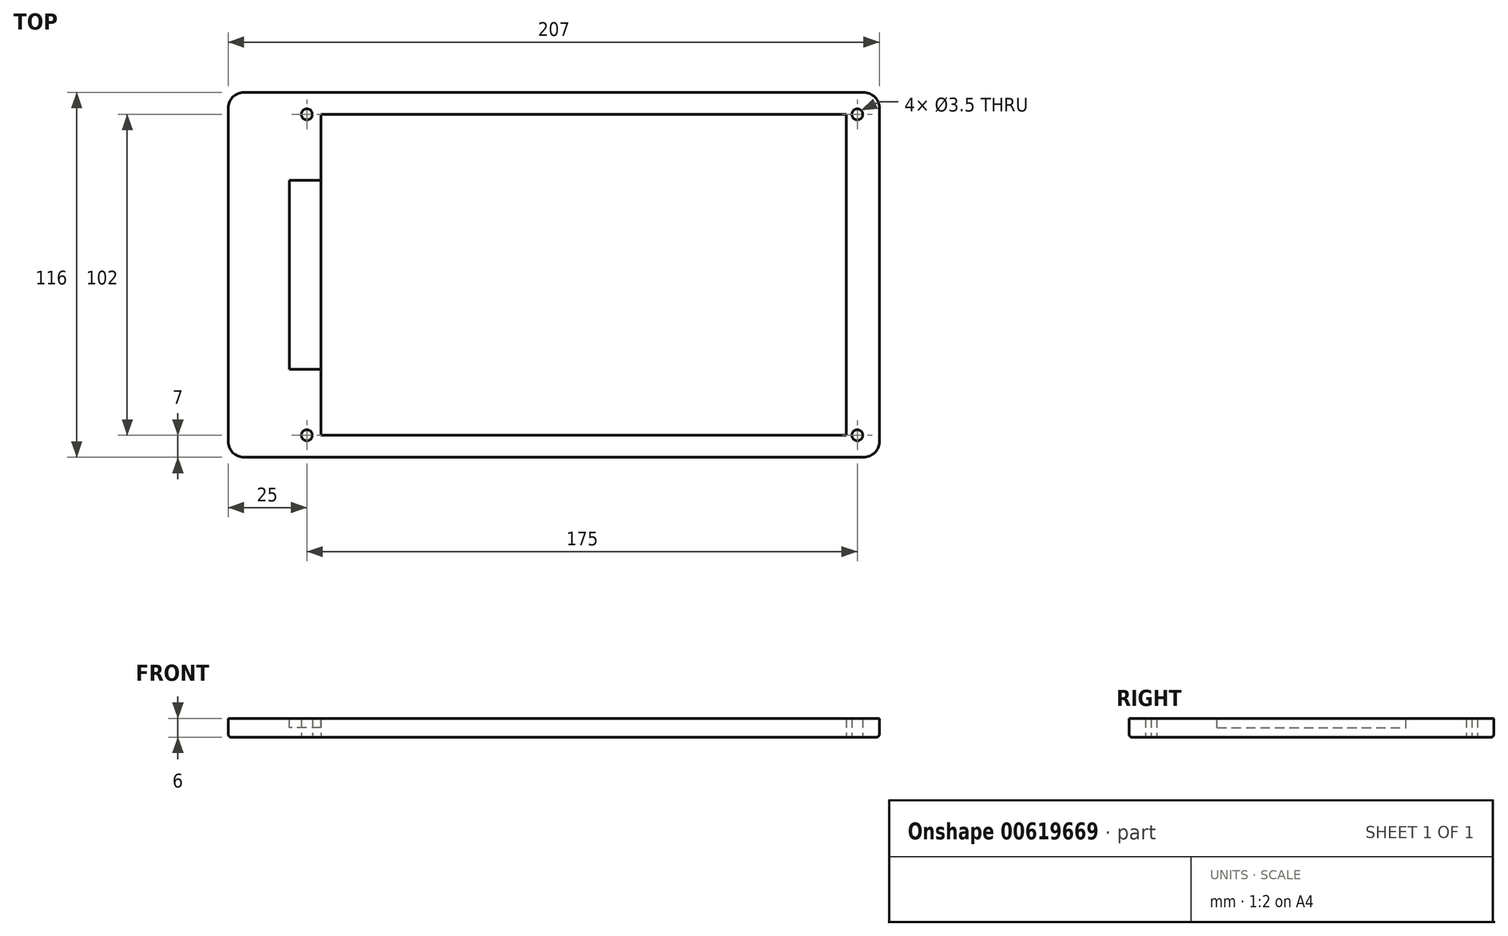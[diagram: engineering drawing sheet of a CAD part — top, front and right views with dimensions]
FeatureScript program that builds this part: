
annotation { "Feature Type Name" : "Feature", "Feature Type Description" : "" }
export const myFeature = defineFeature(function(context is Context, id is Id, definition is map)
    precondition{}
    {
        {
            var Q0;
            Q0=qCreatedBy(makeId("Top.planeOp"),FACE);
            var sketch = newSketch(context, id + "F0", { "sketchPlane" : qUnion([Q0])});
            skLineSegment(sketch, "E0.bottom", {"start": v(0, 0) * mm, "end": v(207, 0) * mm});
            skLineSegment(sketch, "E0.top", {"start": v(0, -116) * mm, "end": v(207, -116) * mm});
            skLineSegment(sketch, "E0.left", {"start": v(0, 0) * mm, "end": v(0, -116) * mm});
            skLineSegment(sketch, "E0.right", {"start": v(207, 0) * mm, "end": v(207, -116) * mm});
            skSolve(sketch);
        }
        {
            var Q0;
            Q0=makeQuery(id+"F0.imprint","IMPRINT",FACE,{"disambiguationData":[TD([[makeQuery(id+"F0.imprint","IMPRINT",EDGE,{"derivedFrom":sQuery(id+"F0.wireOp",EDGE,"E0.bottom")}),-1.0]])]});
            extrude(context, id + "F1", {"entities" : qUnion([Q0]), "depth" : 6 * mm, "offsetDistance" : 25 * mm});
        }
        {
            var Q0;
            Q0=makeQuery(id+"F0.imprint","IMPRINT",FACE,{"disambiguationData":[TD([[makeQuery(id+"F0.imprint","IMPRINT",EDGE,{"derivedFrom":sQuery(id+"F0.wireOp",EDGE,"E0.bottom")}),-1.0]])]});
            var sketch = newSketch(context, id + "F2", { "sketchPlane" : qUnion([Q0])});
            skLineSegment(sketch, "E1.bottom", {"start": v(29.5, -7) * mm, "end": v(196.5, -7) * mm});
            skLineSegment(sketch, "E1.top", {"start": v(29.5, -109) * mm, "end": v(196.5, -109) * mm});
            skLineSegment(sketch, "E1.left", {"start": v(29.5, -7) * mm, "end": v(29.5, -109) * mm});
            skLineSegment(sketch, "E1.right", {"start": v(196.5, -7) * mm, "end": v(196.5, -109) * mm});
            skSolve(sketch);
        }
        {
            var Q0;
            Q0=makeQuery(id+"F2.imprint","IMPRINT",FACE,{"disambiguationData":[TD([[makeQuery(id+"F2.imprint","IMPRINT",EDGE,{"derivedFrom":sQuery(id+"F2.wireOp",EDGE,"E1.bottom")}),-1.0]])]});
            extrude(context, id + "F3", {"entities" : qUnion([Q0]), "operationType" : NewBodyOperationType.REMOVE, "depth" : 25 * mm, "offsetDistance" : 25 * mm});
        }
        {
            var Q0;
            Q0=makeQuery(id+"F1.opExtrude","CAP_FACE",FACE,{"disambiguationData":[OSD([sQuery(id+"F0.wireOp",EDGE,"E0.bottom"),sQuery(id+"F0.wireOp",EDGE,"E0.top"),sQuery(id+"F0.wireOp",EDGE,"E0.left"),sQuery(id+"F0.wireOp",EDGE,"E0.right")])],"isStart":true});
            var sketch = newSketch(context, id + "F4", { "sketchPlane" : qUnion([Q0])});
            skLineSegment(sketch, "E2", {"start": v(207, 7) * mm, "end": v(0, 7) * mm, "construction": true});
            skCircle(sketch, "E3", {"center": v(200, 7) * mm, "radius": 1.75 * mm});
            skCircle(sketch, "E4", {"center": v(25, 7) * mm, "radius": 1.75 * mm});
            skLineSegment(sketch, "E5", {"start": v(207, 109) * mm, "end": v(0, 109) * mm, "construction": true});
            skCircle(sketch, "E6", {"center": v(200, 109) * mm, "radius": 1.75 * mm});
            skCircle(sketch, "E7", {"center": v(25, 109) * mm, "radius": 1.75 * mm});
            skSolve(sketch);
        }
        {
            var Q0;
            Q0=makeQuery(id+"F4.imprint","IMPRINT",FACE,{"disambiguationData":[TD([[makeQuery(id+"F4.imprint","IMPRINT",EDGE,{"derivedFrom":sQuery(id+"F4.wireOp",EDGE,"E3")}),1.0]])]});
            var Q1;
            Q1=makeQuery(id+"F4.imprint","IMPRINT",FACE,{"disambiguationData":[TD([[makeQuery(id+"F4.imprint","IMPRINT",EDGE,{"derivedFrom":sQuery(id+"F4.wireOp",EDGE,"E6")}),1.0]])]});
            var Q2;
            Q2=makeQuery(id+"F4.imprint","IMPRINT",FACE,{"disambiguationData":[TD([[makeQuery(id+"F4.imprint","IMPRINT",EDGE,{"derivedFrom":sQuery(id+"F4.wireOp",EDGE,"E7")}),1.0]])]});
            var Q3;
            Q3=makeQuery(id+"F4.imprint","IMPRINT",FACE,{"disambiguationData":[TD([[makeQuery(id+"F4.imprint","IMPRINT",EDGE,{"derivedFrom":sQuery(id+"F4.wireOp",EDGE,"E4")}),1.0]])]});
            extrude(context, id + "F5", {"entities" : qUnion([Q0, Q1, Q2, Q3]), "operationType" : NewBodyOperationType.REMOVE, "oppositeDirection" : true, "depth" : 25 * mm, "offsetDistance" : 25 * mm});
        }
        {
            var Q0;
            Q0=makeQuery(id+"F1.opExtrude","SWEPT_EDGE",EDGE,{"disambiguationData":[OSD([sQuery(id+"F0.wireOp",EDGE,"E0.bottom"),sQuery(id+"F0.wireOp",EDGE,"E0.right")])]});
            var Q1;
            Q1=makeQuery(id+"F1.opExtrude","SWEPT_EDGE",EDGE,{"disambiguationData":[OSD([sQuery(id+"F0.wireOp",EDGE,"E0.top"),sQuery(id+"F0.wireOp",EDGE,"E0.right")])]});
            var Q2;
            Q2=makeQuery(id+"F1.opExtrude","SWEPT_EDGE",EDGE,{"disambiguationData":[OSD([sQuery(id+"F0.wireOp",EDGE,"E0.top"),sQuery(id+"F0.wireOp",EDGE,"E0.left")])]});
            var Q3;
            Q3=makeQuery(id+"F1.opExtrude","SWEPT_EDGE",EDGE,{"disambiguationData":[OSD([sQuery(id+"F0.wireOp",EDGE,"E0.bottom"),sQuery(id+"F0.wireOp",EDGE,"E0.left")])]});
            fillet(context, id + "F6", {"entities" : qUnion([Q0, Q1, Q2, Q3]), "radius" : 5 * mm, "tangentPropagation" : true, "allowEdgeOverflow" : false});
        }
        {
            var Q0;
            Q0=makeQuery(id+"F1.opExtrude","CAP_EDGE",EDGE,{"disambiguationData":[OSD([sQuery(id+"F0.wireOp",EDGE,"E0.right")])],"isStart":true});
            var Q1;
            Q1=makeQuery(id+"F5.boolean.opBoolean","COPY",EDGE,{"derivedFrom":makeQuery(id+"F5.opExtrude","CAP_EDGE",EDGE,{"disambiguationData":[OSD([sQuery(id+"F4.wireOp",EDGE,"E3")])],"isStart":true})});
            fillet(context, id + "F7", {"entities" : qUnion([Q0, Q1]), "radius" : 1 * mm, "tangentPropagation" : true, "allowEdgeOverflow" : false});
        }
        {
            var Q0;
            Q0=makeQuery(id+"F1.opExtrude","CAP_FACE",FACE,{"disambiguationData":[OSD([sQuery(id+"F0.wireOp",EDGE,"E0.bottom"),sQuery(id+"F0.wireOp",EDGE,"E0.top"),sQuery(id+"F0.wireOp",EDGE,"E0.left"),sQuery(id+"F0.wireOp",EDGE,"E0.right")])],"isStart":false});
            var sketch = newSketch(context, id + "F8", { "sketchPlane" : qUnion([Q0])});
            skLineSegment(sketch, "E8.bottom", {"start": v(29.5, -28) * mm, "end": v(19.5, -28) * mm});
            skLineSegment(sketch, "E8.top", {"start": v(29.5, -88) * mm, "end": v(19.5, -88) * mm});
            skLineSegment(sketch, "E8.left", {"start": v(29.5, -28) * mm, "end": v(29.5, -88) * mm});
            skLineSegment(sketch, "E8.right", {"start": v(19.5, -28) * mm, "end": v(19.5, -88) * mm});
            skSolve(sketch);
        }
        {
            var Q0;
            Q0=makeQuery(id+"F8.imprint","IMPRINT",FACE,{"disambiguationData":[TD([[makeQuery(id+"F8.imprint","IMPRINT",EDGE,{"derivedFrom":sQuery(id+"F8.wireOp",EDGE,"E8.bottom")}),1.0]])]});
            extrude(context, id + "F9", {"entities" : qUnion([Q0]), "operationType" : NewBodyOperationType.REMOVE, "oppositeDirection" : true, "depth" : 3 * mm, "offsetDistance" : 25 * mm});
        }
    });
